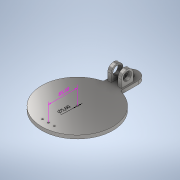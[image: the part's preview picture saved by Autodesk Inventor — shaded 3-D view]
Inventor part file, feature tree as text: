
AUTODESK INVENTOR PART (.ipt)
format: ipt  version: 2021 (Build 250183000, 183)  size: 397,824 bytes
history: native  units: mm
features: extrude x24, sketch x24, other x3, thicken_offset x2, fillet x2
ambient origin geometry x8: Origin, YZ Plane, XZ Plane, XY Plane, X Axis, Y Axis, Z Axis, Center Point
bodies: Solid1 (feature_tree)
feature tree (55):
  other  "Annotations"
  extrude  "Extrusion1"  Depth=10.0mm TaperAngle=0.0deg
  extrude  "Extrusion2"  Depth=20.0mm
  extrude  "Extrusion3"  Depth=17.5mm
  extrude  "Extrusion4"  Depth=5.0mm
  extrude  "Extrusion5"  Depth=10.0mm TaperAngle=0.0deg
  extrude  "Extrusion6"  Depth=10.0mm TaperAngle=0.0deg
  extrude  "Extrusion7"  Depth=15.0mm
  extrude  "Extrusion8"  Depth=30.0mm
  thicken_offset  "Thicken1"
  thicken_offset  "Thicken2"
  extrude  "Extrusion9"  Depth=15.0mm
  sketch  "Sketch11"  dims[d26=30.0mm d27=0.0mm d28=25.0mm]
  extrude  "Extrusion10"  Depth=25.0mm
  extrude  "Extrusion11"  Depth=15.0mm
  extrude  "Extrusion12"  Depth=30.0mm TaperAngle=0.0deg
  extrude  "Extrusion13"  Depth=15.0mm TaperAngle=0.0deg
  extrude  "Extrusion14"  Depth=15.0mm
  extrude  "Extrusion15"  Depth=10.0mm
  extrude  "Extrusion16"  Depth=10.0mm
  sketch  "Sketch18"  dims[d47=10.0mm d48=35.0mm]
  extrude  "Extrusion17"  Depth=35.0mm
  extrude  "Extrusion18"  Depth=5.0mm
  extrude  "Extrusion19"  Depth=5.0mm
  extrude  "Extrusion20"  Depth=25.0mm
  fillet  "Fillet2"  Radius=25.0mm
  extrude  "Extrusion21"  Depth=35.0mm
  extrude  "Extrusion22"  Depth=40.0mm
  extrude  "Extrusion23"  Depth=40.0mm TaperAngle=0.0deg
  fillet  "Fillet3"  Radius=10.0mm
  extrude  "Extrusion24"  Depth=5.0mm TaperAngle=0.0deg
  sketch  "Sketch1"  dims[d0=210.0mm d1=10.0mm d2=0.0mm]
  sketch  "Sketch2"  dims[d4=80.0mm d5=20.0mm]
  sketch  "Sketch3"  dims[d6=17.5mm d7=17.5mm]
  sketch  "Sketch4"  dims[d8=5.0mm d9=5.0mm]
  sketch  "Sketch5"  dims[d10=5.0mm d11=10.0mm d12=0.0mm]
  sketch  "Sketch6"  dims[d13=5.0mm d14=10.0mm d15=0.0mm]
  sketch  "Sketch7"  dims[d20=15.0mm d21=15.0mm]
  sketch  "Sketch8"  dims[d22=30.0mm d23=30.0mm]
  sketch  "Sketch10"  dims[d24=7.5mm d25=15.0mm]
  sketch  "Sketch12"  dims[d29=15.0mm d30=15.0mm]
  sketch  "Sketch13"  dims[d31=180.0deg d32=30.0mm d33=0.0mm]
  sketch  "Sketch14"  dims[d34=10.0mm d35=15.0mm d36=0.0mm]
  sketch  "Sketch15"  dims[d37=15.0mm d38=0.0mm d42=100.0mm]
  sketch  "Sketch16"  dims[d43=10.0mm d44=10.0mm]
  sketch  "Sketch17"  dims[d45=35.0mm d46=10.0mm]
  sketch  "Sketch19"  dims[d49=35.0mm d50=0.0mm d56=5.0mm]
  sketch  "Sketch20"  dims[d57=5.0mm d58=5.0mm]
  sketch  "Sketch22"  dims[d59=5.0mm d60=22.5mm d61=25.0mm]
  sketch  "Sketch23"  dims[d62=40.0mm d63=0.0mm d73=35.0mm]
  sketch  "Sketch24"  dims[d74=35.0mm d75=40.0mm d78=35.0mm]
  sketch  "Sketch25"  dims[d79=40.0mm d80=0.0mm d81=40.0mm d82=0.0mm d83=10.0mm]
  sketch  "Sketch26"  dims[d84=20.0mm d85=150.0mm d86=0.0mm d87=150.0mm d88=0.0mm d89=100.0mm d90=20.0mm d91=35.0mm d92=10.0mm d93=20.0mm d94=10.0mm d95=35.0mm d96=10.0mm d97=40.0mm d98=0.0mm d99=17.5mm d100=25.0mm d101=40.0mm d102=0.0mm d115=50.0mm d116=40.0mm d117=10.0mm d118=0.0mm d120=20.0mm d121=20.0mm d122=5.0mm d123=5.0mm d124=5.0mm d125=10.0mm d126=0.0mm d127=10.0mm d128=0.0mm d132=10.0mm d133=0.0mm d137=25.0mm d138=25.0mm d139=50.0mm d140=25.0mm d141=15.0mm d142=30.0mm d143=25.0mm d144=10.0mm d145=10.0mm d146=0.0mm d147=5.0mm d148=10.0mm d149=0.0mm d150=40.0mm d151=0.0mm d153=10.0mm d154=35.0mm d155=10.0mm d157=10.0mm d158=40.0mm d159=0.0mm d160=17.5mm d161=25.0mm d162=40.0mm d163=0.0mm d131=85.0mm d16=46.771507mm d17=5.0mm]
  other  "Diameter Dimension 1"
  other  "Linear Dimension 6"
